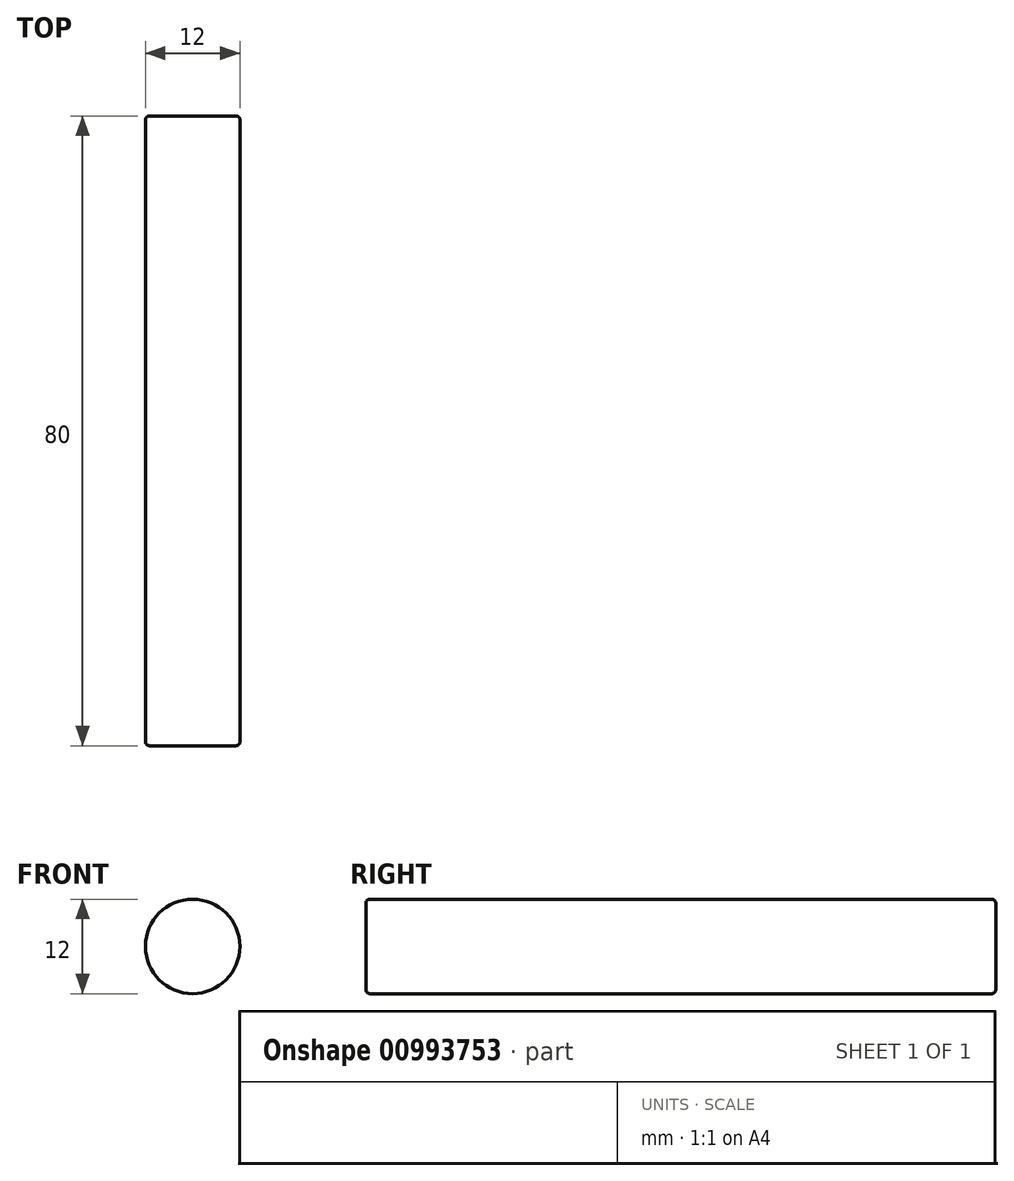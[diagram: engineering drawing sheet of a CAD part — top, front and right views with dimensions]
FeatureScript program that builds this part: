
annotation { "Feature Type Name" : "Feature", "Feature Type Description" : "" }
export const myFeature = defineFeature(function(context is Context, id is Id, definition is map)
    precondition{}
    {
        {
            var Q0;
            Q0=qCreatedBy(makeId("Front.planeOp"),FACE);
            var sketch = newSketch(context, id + "F0", { "sketchPlane" : qUnion([Q0])});
            skCircle(sketch, "E0", {"center": v(0, 0) * mm, "radius": 6 * mm});
            skSolve(sketch);
        }
        {
            var Q0;
            Q0=qSketchRegion(id+"F0",true);
            var Q1;
            Q1=makeQuery(id+"F0.imprint","IMPRINT",FACE,{"disambiguationData":[TD([[makeQuery(id+"F0.imprint","IMPRINT",EDGE,{"derivedFrom":sQuery(id+"F0.wireOp",EDGE,"E0")}),1.0]])]});
            extrude(context, id + "F1", {"entities" : qUnion([Q0, Q1]), "depth" : 80 * mm, "offsetDistance" : 25 * mm});
        }
        {
            var Q0;
            Q0=makeQuery(id+"F1.opExtrude","CAP_EDGE",EDGE,{"disambiguationData":[OSD([sQuery(id+"F0.wireOp",EDGE,"E0")])],"isStart":false});
            var Q1;
            Q1=makeQuery(id+"F1.opExtrude","CAP_EDGE",EDGE,{"disambiguationData":[OSD([sQuery(id+"F0.wireOp",EDGE,"E0")])],"isStart":true});
            fillet(context, id + "F2", {"entities" : qUnion([Q0, Q1]), "radius" : 0.5 * mm, "tangentPropagation" : true, "allowEdgeOverflow" : false});
        }
    });
